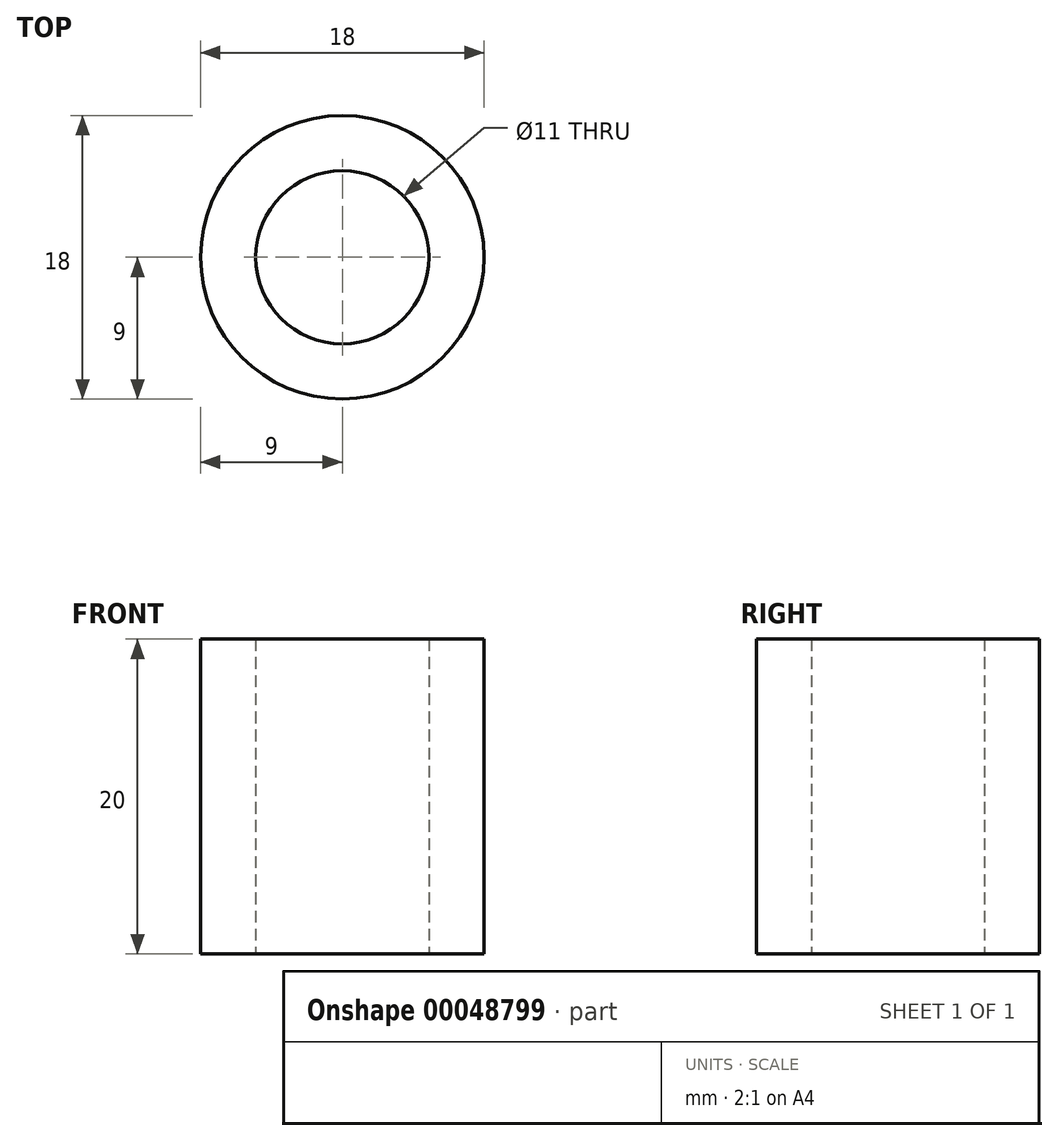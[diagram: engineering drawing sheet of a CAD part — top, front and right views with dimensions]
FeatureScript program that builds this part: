
annotation { "Feature Type Name" : "Feature", "Feature Type Description" : "" }
export const myFeature = defineFeature(function(context is Context, id is Id, definition is map)
    precondition{}
    {
        {
            var Q0;
            Q0=qCreatedBy(makeId("Top.planeOp"),FACE);
            var sketch = newSketch(context, id + "F0", { "sketchPlane" : qUnion([Q0])});
            skCircle(sketch, "E0", {"center": v(0, 0) * mm, "radius": 5.5 * mm});
            skCircle(sketch, "E1", {"center": v(0, 0) * mm, "radius": 9 * mm});
            skSolve(sketch);
        }
        {
            assignVariable(context, id + "F1", {"variableType" : VariableType.LENGTH, "name" : "Height", "lengthValue" : 20 * mm});
        }
        {
            var Q0;
            Q0=makeQuery(id+"F0.imprint","IMPRINT",FACE,{"disambiguationData":[TD([[makeQuery(id+"F0.imprint","IMPRINT",EDGE,{"derivedFrom":sQuery(id+"F0.wireOp",EDGE,"E0")}),-1.0]])]});
            extrude(context, id + "F2", {"entities" : qUnion([Q0]), "flatOperationType" : FlatOperationType.REMOVE, "offsetDistance" : 25 * mm, "depth" : getVariable(context, 'Height'), "domain" : OperationDomain.MODEL});
        }
    });
